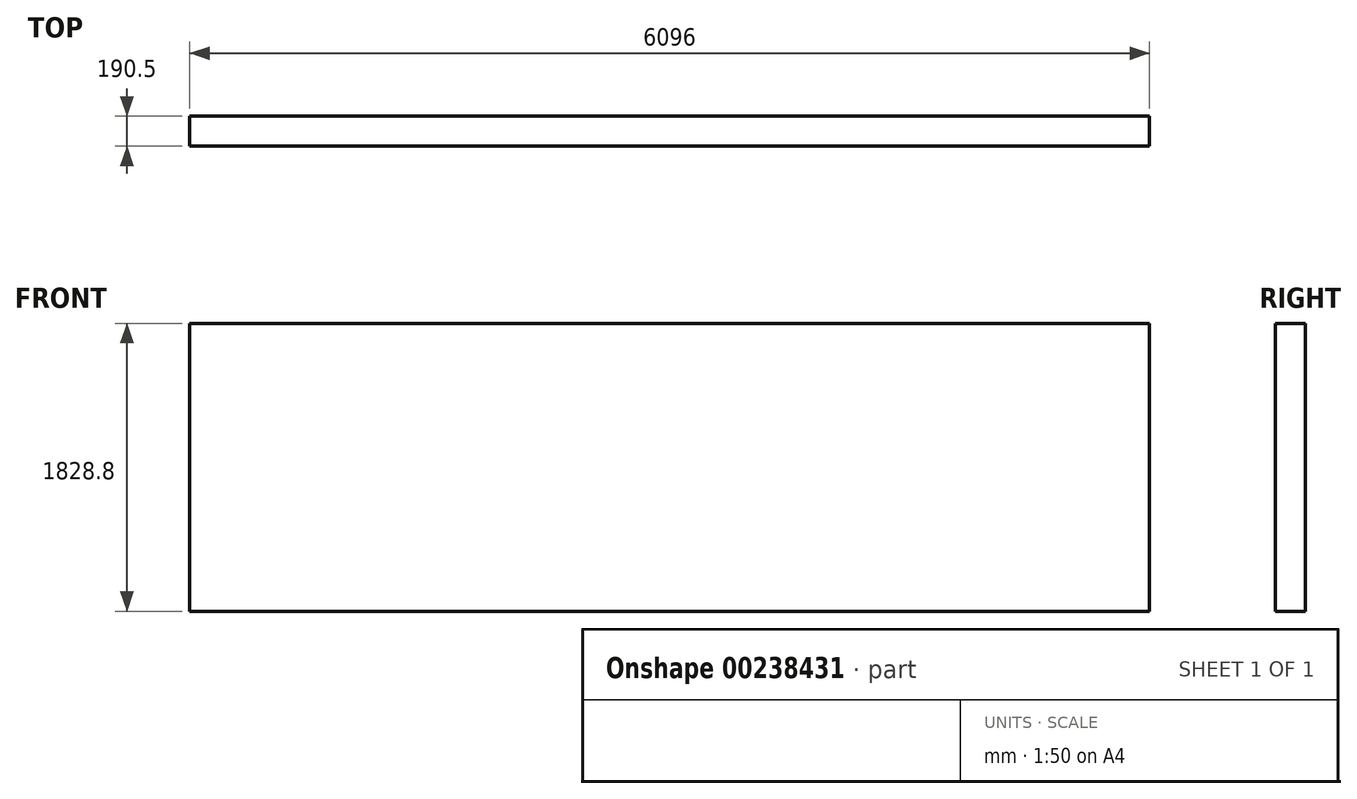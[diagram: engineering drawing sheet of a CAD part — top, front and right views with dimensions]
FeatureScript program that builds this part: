
annotation { "Feature Type Name" : "Feature", "Feature Type Description" : "" }
export const myFeature = defineFeature(function(context is Context, id is Id, definition is map)
    precondition{}
    {
        {
            var Q0;
            Q0=qCreatedBy(makeId("Front.planeOp"),FACE);
            var sketch = newSketch(context, id + "F0", { "sketchPlane" : qUnion([Q0])});
            skLineSegment(sketch, "E0.bottom", {"start": v(-3085.5, -196) * mm, "end": v(3010.5, -196) * mm});
            skLineSegment(sketch, "E0.top", {"start": v(-3085.5, -2024.8) * mm, "end": v(3010.5, -2024.8) * mm});
            skLineSegment(sketch, "E0.left", {"start": v(-3085.5, -196) * mm, "end": v(-3085.5, -2024.8) * mm});
            skLineSegment(sketch, "E0.right", {"start": v(3010.5, -196) * mm, "end": v(3010.5, -2024.8) * mm});
            skSolve(sketch);
        }
        {
            var Q0;
            Q0=makeQuery(id+"F0.imprint","IMPRINT",FACE,{"disambiguationData":[TD([[makeQuery(id+"F0.imprint","IMPRINT",EDGE,{"derivedFrom":sQuery(id+"F0.wireOp",EDGE,"E0.bottom")}),-1.0]])]});
            extrude(context, id + "F1", {"entities" : qUnion([Q0]), "depth" : 190.5 * mm});
        }
    });
